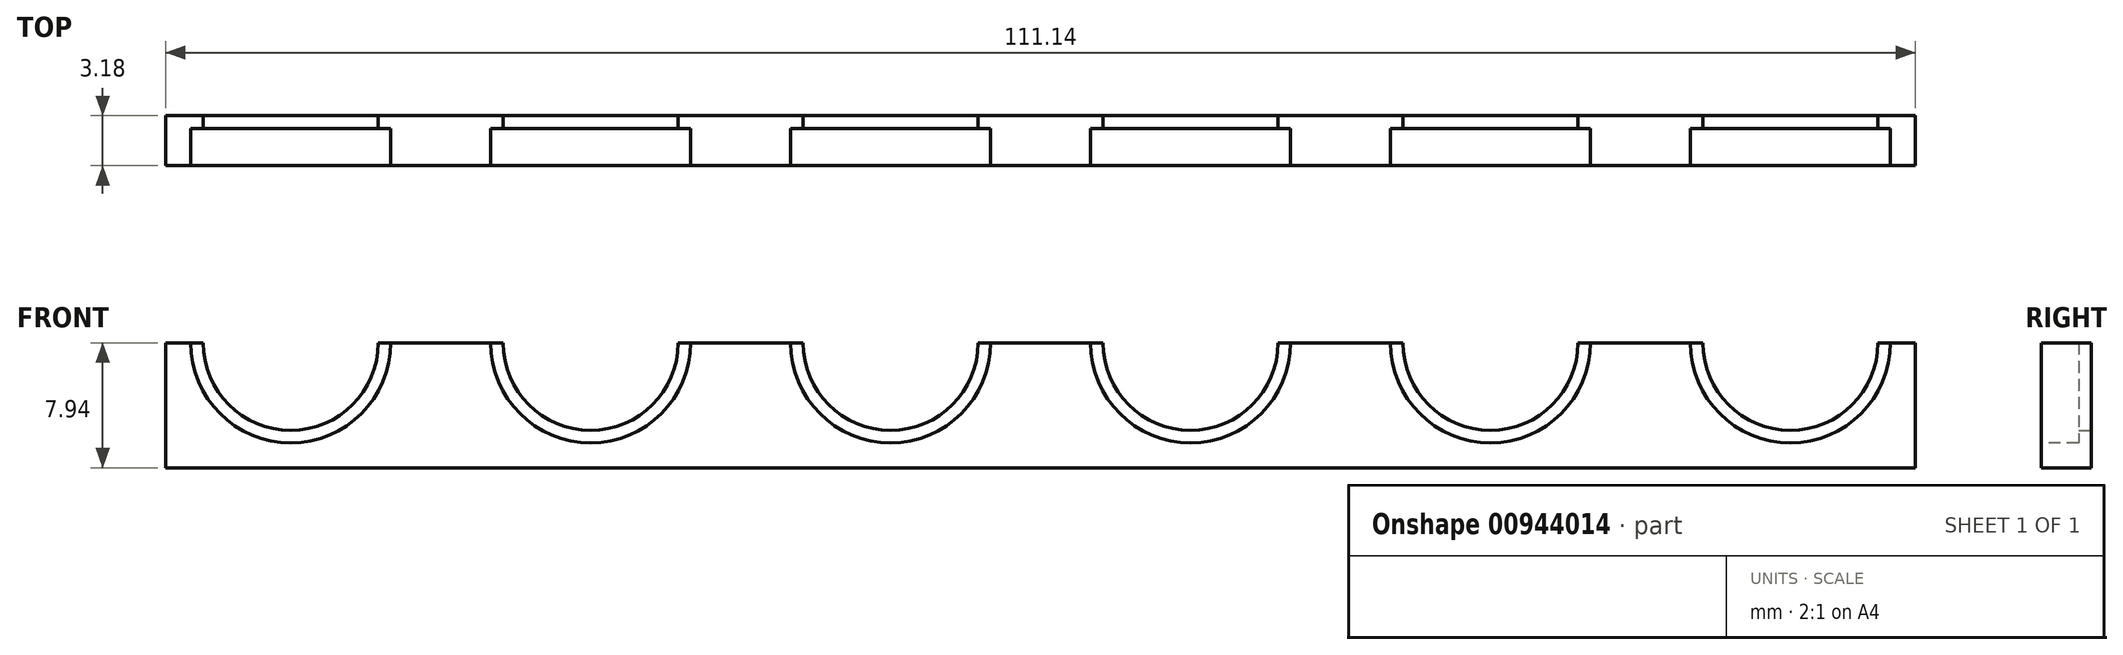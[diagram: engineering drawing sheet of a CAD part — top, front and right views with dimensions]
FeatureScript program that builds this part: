
annotation { "Feature Type Name" : "Feature", "Feature Type Description" : "" }
export const myFeature = defineFeature(function(context is Context, id is Id, definition is map)
    precondition{}
    {
        {
            var Q0;
            Q0=qCreatedBy(makeId("Front.planeOp"),FACE);
            var sketch = newSketch(context, id + "F0", { "sketchPlane" : qUnion([Q0])});
            skLineSegment(sketch, "E0", {"start": v(0, 0) * mm, "end": v(-6.35, 0) * mm});
            skLineSegment(sketch, "E1", {"start": v(-6.35, 0) * mm, "end": v(-7.94, 0) * mm});
            skLineSegment(sketch, "E2", {"start": v(-7.94, 0) * mm, "end": v(-11.11, 0) * mm});
            skLineSegment(sketch, "E3", {"start": v(-11.11, 0) * mm, "end": v(-12.7, 0) * mm});
            skLineSegment(sketch, "E4", {"start": v(-12.7, 0) * mm, "end": v(-19.05, 0) * mm});
            skLineSegment(sketch, "E5", {"start": v(-19.05, 0) * mm, "end": v(-25.4, 0) * mm});
            skLineSegment(sketch, "E6", {"start": v(-25.4, 0) * mm, "end": v(-26.99, 0) * mm});
            skLineSegment(sketch, "E7", {"start": v(-26.99, 0) * mm, "end": v(-30.16, 0) * mm});
            skLineSegment(sketch, "E8", {"start": v(-30.16, 0) * mm, "end": v(-31.75, 0) * mm});
            skLineSegment(sketch, "E9", {"start": v(-31.75, 0) * mm, "end": v(-38.1, 0) * mm});
            skLineSegment(sketch, "E10", {"start": v(-38.1, 0) * mm, "end": v(-44.45, 0) * mm});
            skLineSegment(sketch, "E11", {"start": v(-44.45, 0) * mm, "end": v(-46.04, 0) * mm});
            skLineSegment(sketch, "E12", {"start": v(-46.04, 0) * mm, "end": v(-49.21, 0) * mm});
            skLineSegment(sketch, "E13", {"start": v(-49.21, 0) * mm, "end": v(-50.8, 0) * mm});
            skLineSegment(sketch, "E14", {"start": v(-50.8, 0) * mm, "end": v(-57.15, 0) * mm});
            skLineSegment(sketch, "E15", {"start": v(-57.15, 0) * mm, "end": v(-63.5, 0) * mm});
            skLineSegment(sketch, "E16", {"start": v(-63.5, 0) * mm, "end": v(-65.09, 0) * mm});
            skLineSegment(sketch, "E17", {"start": v(-65.09, 0) * mm, "end": v(-68.26, 0) * mm});
            skLineSegment(sketch, "E18", {"start": v(-68.26, 0) * mm, "end": v(-69.85, 0) * mm});
            skLineSegment(sketch, "E19", {"start": v(-69.85, 0) * mm, "end": v(-76.2, 0) * mm});
            skLineSegment(sketch, "E20", {"start": v(-76.2, 0) * mm, "end": v(-82.55, 0) * mm});
            skLineSegment(sketch, "E21", {"start": v(-82.55, 0) * mm, "end": v(-84.14, 0) * mm});
            skLineSegment(sketch, "E22", {"start": v(-84.14, 0) * mm, "end": v(-87.31, 0) * mm});
            skLineSegment(sketch, "E23", {"start": v(-87.31, 0) * mm, "end": v(-88.9, 0) * mm});
            skLineSegment(sketch, "E24", {"start": v(-88.9, 0) * mm, "end": v(-95.25, 0) * mm});
            skLineSegment(sketch, "E25", {"start": v(-95.25, 0) * mm, "end": v(-101.6, 0) * mm});
            skLineSegment(sketch, "E26", {"start": v(-101.6, 0) * mm, "end": v(-103.2, 0) * mm});
            skLineSegment(sketch, "E27", {"start": v(0, 0) * mm, "end": v(6.35, 0) * mm});
            skLineSegment(sketch, "E28", {"start": v(6.35, 0) * mm, "end": v(7.94, 0) * mm});
            skCircle(sketch, "E29", {"center": v(0, 0) * mm, "radius": 6.35 * mm});
            skCircle(sketch, "E30", {"center": v(0, 0) * mm, "radius": 7.94 * mm});
            skCircle(sketch, "E31", {"center": v(-19.05, 0) * mm, "radius": 6.35 * mm});
            skCircle(sketch, "E32", {"center": v(-19.05, 0) * mm, "radius": 7.94 * mm});
            skCircle(sketch, "E33", {"center": v(-38.1, 0) * mm, "radius": 6.35 * mm});
            skCircle(sketch, "E34", {"center": v(-38.1, 0) * mm, "radius": 7.94 * mm});
            skCircle(sketch, "E35", {"center": v(-57.15, 0) * mm, "radius": 6.35 * mm});
            skCircle(sketch, "E36", {"center": v(-57.15, 0) * mm, "radius": 7.94 * mm});
            skCircle(sketch, "E37", {"center": v(-76.2, 0) * mm, "radius": 6.35 * mm});
            skCircle(sketch, "E38", {"center": v(-76.2, 0) * mm, "radius": 7.94 * mm});
            skCircle(sketch, "E39", {"center": v(-95.25, 0) * mm, "radius": 6.35 * mm});
            skCircle(sketch, "E40", {"center": v(-95.25, 0) * mm, "radius": 7.94 * mm});
            skLineSegment(sketch, "E41", {"start": v(-95.25, 0) * mm, "end": v(-95.25, -7.94) * mm});
            skLineSegment(sketch, "E42", {"start": v(0, 0) * mm, "end": v(0, -7.94) * mm});
            skLineSegment(sketch, "E43", {"start": v(-103.2, 0) * mm, "end": v(-103.2, -7.94) * mm});
            skLineSegment(sketch, "E44", {"start": v(7.94, 0) * mm, "end": v(7.94, -7.94) * mm});
            skLineSegment(sketch, "E45", {"start": v(7.94, -7.94) * mm, "end": v(-103.2, -7.94) * mm});
            skLineSegment(sketch, "E46", {"start": v(-101.6, 0) * mm, "end": v(-100.8, 0) * mm});
            skCircle(sketch, "E47", {"center": v(-95.25, 0) * mm, "radius": 5.56 * mm});
            skLineSegment(sketch, "E48", {"start": v(-82.55, 0) * mm, "end": v(-81.76, 0) * mm});
            skCircle(sketch, "E49", {"center": v(-76.2, 0) * mm, "radius": 5.56 * mm});
            skLineSegment(sketch, "E50", {"start": v(-63.5, 0) * mm, "end": v(-62.7, 0) * mm});
            skCircle(sketch, "E51", {"center": v(-57.15, 0) * mm, "radius": 5.56 * mm});
            skLineSegment(sketch, "E52", {"start": v(-44.45, 0) * mm, "end": v(-43.66, 0) * mm});
            skCircle(sketch, "E53", {"center": v(-38.1, 0) * mm, "radius": 5.56 * mm});
            skLineSegment(sketch, "E54", {"start": v(-25.4, 0) * mm, "end": v(-24.6, 0) * mm});
            skCircle(sketch, "E55", {"center": v(-19.05, 0) * mm, "radius": 5.56 * mm});
            skLineSegment(sketch, "E56", {"start": v(-6.35, 0) * mm, "end": v(-5.56, 0) * mm});
            skCircle(sketch, "E57", {"center": v(0, 0) * mm, "radius": 5.56 * mm});
            skSolve(sketch);
        }
        {
            var Q0;
            {var subQ0=sQuery(id+"F0.wireOp",EDGE,"E43");Q0=makeQuery(id+"F0.imprint","IMPRINT",FACE,{"disambiguationData":[TD([[makeQuery(id+"F0.imprint","IMPRINT",EDGE,{"derivedFrom":subQ0}),1.0]])]});}
            var Q1;
            {var subQ0=sQuery(id+"F0.wireOp",EDGE,"E44");Q1=makeQuery(id+"F0.imprint","IMPRINT",FACE,{"disambiguationData":[TD([[makeQuery(id+"F0.imprint","IMPRINT",EDGE,{"derivedFrom":subQ0}),-1.0]])]});}
            var Q2;
            {var subQ0=sQuery(id+"F0.wireOp",EDGE,"E2");Q2=makeQuery(id+"F0.imprint","IMPRINT",FACE,{"disambiguationData":[TD([[makeQuery(id+"F0.imprint","IMPRINT",EDGE,{"derivedFrom":subQ0}),1.0]])]});}
            var Q3;
            {var subQ0=sQuery(id+"F0.wireOp",EDGE,"E7");Q3=makeQuery(id+"F0.imprint","IMPRINT",FACE,{"disambiguationData":[TD([[makeQuery(id+"F0.imprint","IMPRINT",EDGE,{"derivedFrom":subQ0}),1.0]])]});}
            var Q4;
            {var subQ0=sQuery(id+"F0.wireOp",EDGE,"E12");Q4=makeQuery(id+"F0.imprint","IMPRINT",FACE,{"disambiguationData":[TD([[makeQuery(id+"F0.imprint","IMPRINT",EDGE,{"derivedFrom":subQ0}),1.0]])]});}
            var Q5;
            {var subQ0=sQuery(id+"F0.wireOp",EDGE,"E17");Q5=makeQuery(id+"F0.imprint","IMPRINT",FACE,{"disambiguationData":[TD([[makeQuery(id+"F0.imprint","IMPRINT",EDGE,{"derivedFrom":subQ0}),1.0]])]});}
            var Q6;
            {var subQ0=sQuery(id+"F0.wireOp",EDGE,"E22");Q6=makeQuery(id+"F0.imprint","IMPRINT",FACE,{"disambiguationData":[TD([[makeQuery(id+"F0.imprint","IMPRINT",EDGE,{"derivedFrom":subQ0}),1.0]])]});}
            var Q7;
            {var subQ0=sQuery(id+"F0.wireOp",EDGE,"E1");Q7=makeQuery(id+"F0.imprint","IMPRINT",FACE,{"disambiguationData":[TD([[makeQuery(id+"F0.imprint","IMPRINT",EDGE,{"derivedFrom":subQ0}),1.0]])]});}
            var Q8;
            {var subQ1=sQuery(id+"F0.wireOp",EDGE,"E3");Q8=makeQuery(id+"F0.imprint","IMPRINT",FACE,{"disambiguationData":[TD([[makeQuery(id+"F0.imprint","IMPRINT",EDGE,{"derivedFrom":subQ1}),1.0]])]});}
            var Q9;
            {var subQ1=sQuery(id+"F0.wireOp",EDGE,"E8");Q9=makeQuery(id+"F0.imprint","IMPRINT",FACE,{"disambiguationData":[TD([[makeQuery(id+"F0.imprint","IMPRINT",EDGE,{"derivedFrom":subQ1}),1.0]])]});}
            var Q10;
            {var subQ1=sQuery(id+"F0.wireOp",EDGE,"E13");Q10=makeQuery(id+"F0.imprint","IMPRINT",FACE,{"disambiguationData":[TD([[makeQuery(id+"F0.imprint","IMPRINT",EDGE,{"derivedFrom":subQ1}),1.0]])]});}
            var Q11;
            {var subQ1=sQuery(id+"F0.wireOp",EDGE,"E18");Q11=makeQuery(id+"F0.imprint","IMPRINT",FACE,{"disambiguationData":[TD([[makeQuery(id+"F0.imprint","IMPRINT",EDGE,{"derivedFrom":subQ1}),1.0]])]});}
            var Q12;
            {var subQ0=sQuery(id+"F0.wireOp",EDGE,"E23");Q12=makeQuery(id+"F0.imprint","IMPRINT",FACE,{"disambiguationData":[TD([[makeQuery(id+"F0.imprint","IMPRINT",EDGE,{"derivedFrom":subQ0}),1.0]])]});}
            var Q13;
            {var subQ1=sQuery(id+"F0.wireOp",EDGE,"E26");var subQ3=sQuery(id+"F0.wireOp",EDGE,"E40");var subQ4=makeQuery(id+"F0.imprint","INTERSECT",VERTEX,{"derivedFrom":[subQ1,subQ3]});Q13=makeQuery(id+"F0.imprint","IMPRINT",FACE,{"disambiguationData":[TD([[makeQuery(id+"F0.imprint","IMPRINT",EDGE,{"disambiguationData":[TD([[subQ4,1.0]])],"derivedFrom":subQ1}),1.0]])]});}
            var Q14;
            {var subQ0=sQuery(id+"F0.wireOp",EDGE,"E28");Q14=makeQuery(id+"F0.imprint","IMPRINT",FACE,{"disambiguationData":[TD([[makeQuery(id+"F0.imprint","IMPRINT",EDGE,{"derivedFrom":subQ0}),-1.0]])]});}
            var Q15;
            {var subQ1=sQuery(id+"F0.wireOp",EDGE,"E19");var subQ3=sQuery(id+"F0.wireOp",EDGE,"E49");var subQ4=makeQuery(id+"F0.imprint","INTERSECT",VERTEX,{"derivedFrom":[subQ1,subQ3]});Q15=makeQuery(id+"F0.imprint","IMPRINT",FACE,{"disambiguationData":[TD([[makeQuery(id+"F0.imprint","IMPRINT",EDGE,{"disambiguationData":[TD([[subQ4,1.0]])],"derivedFrom":subQ3}),-1.0]])]});}
            var Q16;
            {var subQ1=sQuery(id+"F0.wireOp",EDGE,"E14");var subQ3=sQuery(id+"F0.wireOp",EDGE,"E51");var subQ4=makeQuery(id+"F0.imprint","INTERSECT",VERTEX,{"derivedFrom":[subQ1,subQ3]});Q16=makeQuery(id+"F0.imprint","IMPRINT",FACE,{"disambiguationData":[TD([[makeQuery(id+"F0.imprint","IMPRINT",EDGE,{"disambiguationData":[TD([[subQ4,1.0]])],"derivedFrom":subQ3}),-1.0]])]});}
            var Q17;
            {var subQ1=sQuery(id+"F0.wireOp",EDGE,"E9");var subQ3=sQuery(id+"F0.wireOp",EDGE,"E53");var subQ4=makeQuery(id+"F0.imprint","INTERSECT",VERTEX,{"derivedFrom":[subQ1,subQ3]});Q17=makeQuery(id+"F0.imprint","IMPRINT",FACE,{"disambiguationData":[TD([[makeQuery(id+"F0.imprint","IMPRINT",EDGE,{"disambiguationData":[TD([[subQ4,1.0]])],"derivedFrom":subQ3}),-1.0]])]});}
            var Q18;
            {var subQ1=sQuery(id+"F0.wireOp",EDGE,"E4");var subQ3=sQuery(id+"F0.wireOp",EDGE,"E55");var subQ4=makeQuery(id+"F0.imprint","INTERSECT",VERTEX,{"derivedFrom":[subQ1,subQ3]});Q18=makeQuery(id+"F0.imprint","IMPRINT",FACE,{"disambiguationData":[TD([[makeQuery(id+"F0.imprint","IMPRINT",EDGE,{"disambiguationData":[TD([[subQ4,1.0]])],"derivedFrom":subQ3}),-1.0]])]});}
            var Q19;
            {var subQ0=sQuery(id+"F0.wireOp",EDGE,"E29");var subQ5=sQuery(id+"F0.wireOp",EDGE,"E42");var subQ6=makeQuery(id+"F0.imprint","INTERSECT",VERTEX,{"derivedFrom":[subQ0,subQ5]});Q19=makeQuery(id+"F0.imprint","IMPRINT",FACE,{"disambiguationData":[TD([[makeQuery(id+"F0.imprint","IMPRINT",EDGE,{"disambiguationData":[TD([[subQ6,1.0]])],"derivedFrom":subQ5}),-1.0]])]});}
            var Q20;
            {var subQ0=sQuery(id+"F0.wireOp",EDGE,"E29");var subQ5=sQuery(id+"F0.wireOp",EDGE,"E42");var subQ7=makeQuery(id+"F0.imprint","INTERSECT",VERTEX,{"derivedFrom":[subQ0,subQ5]});Q20=makeQuery(id+"F0.imprint","IMPRINT",FACE,{"disambiguationData":[TD([[makeQuery(id+"F0.imprint","IMPRINT",EDGE,{"disambiguationData":[TD([[subQ7,1.0]])],"derivedFrom":subQ5}),1.0]])]});}
            var Q21;
            {var subQ0=sQuery(id+"F0.wireOp",EDGE,"E39");var subQ5=sQuery(id+"F0.wireOp",EDGE,"E41");var subQ7=makeQuery(id+"F0.imprint","INTERSECT",VERTEX,{"derivedFrom":[subQ0,subQ5]});Q21=makeQuery(id+"F0.imprint","IMPRINT",FACE,{"disambiguationData":[TD([[makeQuery(id+"F0.imprint","IMPRINT",EDGE,{"disambiguationData":[TD([[subQ7,1.0]])],"derivedFrom":subQ5}),1.0]])]});}
            var Q22;
            {var subQ0=sQuery(id+"F0.wireOp",EDGE,"E39");var subQ5=sQuery(id+"F0.wireOp",EDGE,"E41");var subQ6=makeQuery(id+"F0.imprint","INTERSECT",VERTEX,{"derivedFrom":[subQ0,subQ5]});Q22=makeQuery(id+"F0.imprint","IMPRINT",FACE,{"disambiguationData":[TD([[makeQuery(id+"F0.imprint","IMPRINT",EDGE,{"disambiguationData":[TD([[subQ6,1.0]])],"derivedFrom":subQ5}),-1.0]])]});}
            extrude(context, id + "F1", {"entities" : qUnion([Q0, Q1, Q2, Q3, Q4, Q5, Q6, Q7, Q8, Q9, Q10, Q11, Q12, Q13, Q14, Q15, Q16, Q17, Q18, Q19, Q20, Q21, Q22]), "depth" : 3.17 * mm, "offsetDistance" : 25.4 * mm});
        }
        {
            var Q0;
            Q0=makeQuery(id+"F1.opExtrude","CAP_FACE",FACE,{"disambiguationData":[OSD([sQuery(id+"F0.wireOp",EDGE,"E0"),sQuery(id+"F0.wireOp",EDGE,"E1"),sQuery(id+"F0.wireOp",EDGE,"E2"),sQuery(id+"F0.wireOp",EDGE,"E3"),sQuery(id+"F0.wireOp",EDGE,"E4"),sQuery(id+"F0.wireOp",EDGE,"E5"),sQuery(id+"F0.wireOp",EDGE,"E6"),sQuery(id+"F0.wireOp",EDGE,"E7"),sQuery(id+"F0.wireOp",EDGE,"E8"),sQuery(id+"F0.wireOp",EDGE,"E9"),sQuery(id+"F0.wireOp",EDGE,"E10"),sQuery(id+"F0.wireOp",EDGE,"E11"),sQuery(id+"F0.wireOp",EDGE,"E12"),sQuery(id+"F0.wireOp",EDGE,"E13"),sQuery(id+"F0.wireOp",EDGE,"E14"),sQuery(id+"F0.wireOp",EDGE,"E15"),sQuery(id+"F0.wireOp",EDGE,"E16"),sQuery(id+"F0.wireOp",EDGE,"E17"),sQuery(id+"F0.wireOp",EDGE,"E18"),sQuery(id+"F0.wireOp",EDGE,"E19"),sQuery(id+"F0.wireOp",EDGE,"E20"),sQuery(id+"F0.wireOp",EDGE,"E21"),sQuery(id+"F0.wireOp",EDGE,"E22"),sQuery(id+"F0.wireOp",EDGE,"E23"),sQuery(id+"F0.wireOp",EDGE,"E24"),sQuery(id+"F0.wireOp",EDGE,"E25"),sQuery(id+"F0.wireOp",EDGE,"E26"),sQuery(id+"F0.wireOp",EDGE,"E27"),sQuery(id+"F0.wireOp",EDGE,"E28"),sQuery(id+"F0.wireOp",EDGE,"E43"),sQuery(id+"F0.wireOp",EDGE,"E44"),sQuery(id+"F0.wireOp",EDGE,"E45"),sQuery(id+"F0.wireOp",EDGE,"E47"),sQuery(id+"F0.wireOp",EDGE,"E49"),sQuery(id+"F0.wireOp",EDGE,"E51"),sQuery(id+"F0.wireOp",EDGE,"E53"),sQuery(id+"F0.wireOp",EDGE,"E55"),sQuery(id+"F0.wireOp",EDGE,"E57")])],"isStart":false});
            var sketch = newSketch(context, id + "F2", { "sketchPlane" : qUnion([Q0])});
            skLineSegment(sketch, "E58", {"start": v(-100.8, 0) * mm, "end": v(-101.6, 0) * mm});
            skCircle(sketch, "E59", {"center": v(-95.25, 0) * mm, "radius": 6.35 * mm});
            skLineSegment(sketch, "E60", {"start": v(-81.76, 0) * mm, "end": v(-82.55, 0) * mm});
            skCircle(sketch, "E61", {"center": v(-76.2, 0) * mm, "radius": 6.35 * mm});
            skLineSegment(sketch, "E62", {"start": v(-62.7, 0) * mm, "end": v(-63.5, 0) * mm});
            skCircle(sketch, "E63", {"center": v(-57.15, 0) * mm, "radius": 6.35 * mm});
            skLineSegment(sketch, "E64", {"start": v(-43.66, 0) * mm, "end": v(-44.45, 0) * mm});
            skCircle(sketch, "E65", {"center": v(-38.1, 0) * mm, "radius": 6.35 * mm});
            skLineSegment(sketch, "E66", {"start": v(-24.6, 0) * mm, "end": v(-25.4, 0) * mm});
            skCircle(sketch, "E67", {"center": v(-19.05, 0) * mm, "radius": 6.35 * mm});
            skLineSegment(sketch, "E68", {"start": v(-5.56, 0) * mm, "end": v(-6.35, 0) * mm});
            skCircle(sketch, "E69", {"center": v(0, 0) * mm, "radius": 6.35 * mm});
            skSolve(sketch);
        }
        {
            var Q0;
            Q0 = qSketchRegion(id + "F2", true);
            extrude(context, id + "F3", {"entities" : qUnion([Q0]), "operationType" : NewBodyOperationType.REMOVE, "oppositeDirection" : true, "depth" : 2.36 * mm, "offsetDistance" : 25.4 * mm});
        }
        {
            var Q0;
            Q0=makeQuery(id+"F1.opExtrude","SWEPT_FACE",FACE,{"disambiguationData":[OSD([sQuery(id+"F0.wireOp",EDGE,"E44")])]});
            var sketch = newSketch(context, id + "F4", { "sketchPlane" : qUnion([Q0])});
            skLineSegment(sketch, "E70", {"start": v(-3.18, 0) * mm, "end": v(-2.38, 0) * mm});
            skLineSegment(sketch, "E71", {"start": v(-2.38, 0) * mm, "end": v(-2.38, -3.18) * mm});
            skLineSegment(sketch, "E72", {"start": v(-2.38, -3.18) * mm, "end": v(-2.38, -4.76) * mm});
            skLineSegment(sketch, "E73", {"start": v(-2.38, -4.76) * mm, "end": v(-0.8, -4.76) * mm});
            skLineSegment(sketch, "E74", {"start": v(-0.8, -4.76) * mm, "end": v(-0.8, -3.18) * mm});
            skLineSegment(sketch, "E75", {"start": v(-0.8, -3.18) * mm, "end": v(-2.38, -3.18) * mm});
            skLineSegment(sketch, "E76", {"start": v(-0.8, -3.18) * mm, "end": v(-0.8, 0) * mm});
            skLineSegment(sketch, "E77", {"start": v(-0.8, 0) * mm, "end": v(0, 0) * mm});
            skLineSegment(sketch, "E78", {"start": v(0, 0) * mm, "end": v(0, -7.94) * mm});
            skLineSegment(sketch, "E79", {"start": v(0, -7.94) * mm, "end": v(-3.18, -7.94) * mm});
            skLineSegment(sketch, "E80", {"start": v(-3.18, -7.94) * mm, "end": v(-3.18, 0) * mm});
            skSolve(sketch);
        }
        {
            var Q0;
            Q0=makeQuery(id+"F4.imprint","IMPRINT",FACE,{"disambiguationData":[TD([[makeQuery(id+"F4.imprint","IMPRINT",EDGE,{"derivedFrom":sQuery(id+"F4.wireOp",EDGE,"E70")}),-1.0]])]});
            extrude(context, id + "F5", {"entities" : qUnion([Q0]), "operationType" : NewBodyOperationType.ADD, "depth" : 1.59 * mm, "offsetDistance" : 25.4 * mm});
        }
        {
            var Q0;
            Q0=makeQuery(id+"F1.opExtrude","SWEPT_FACE",FACE,{"disambiguationData":[OSD([sQuery(id+"F0.wireOp",EDGE,"E43")])]});
            var sketch = newSketch(context, id + "F6", { "sketchPlane" : qUnion([Q0])});
            skLineSegment(sketch, "E81", {"start": v(0, 0) * mm, "end": v(0.8, 0) * mm});
            skLineSegment(sketch, "E82", {"start": v(0.8, 0) * mm, "end": v(0.8, -3.18) * mm});
            skLineSegment(sketch, "E83", {"start": v(0.8, -3.18) * mm, "end": v(0.8, -4.76) * mm});
            skLineSegment(sketch, "E84", {"start": v(0.8, -4.76) * mm, "end": v(2.38, -4.76) * mm});
            skLineSegment(sketch, "E85", {"start": v(2.38, -4.76) * mm, "end": v(2.38, -3.18) * mm});
            skLineSegment(sketch, "E86", {"start": v(2.38, -3.18) * mm, "end": v(0.8, -3.18) * mm});
            skLineSegment(sketch, "E87", {"start": v(2.38, -3.18) * mm, "end": v(2.38, 0) * mm});
            skLineSegment(sketch, "E88", {"start": v(2.38, 0) * mm, "end": v(3.18, 0) * mm});
            skLineSegment(sketch, "E89", {"start": v(3.18, 0) * mm, "end": v(3.18, -7.94) * mm});
            skLineSegment(sketch, "E90", {"start": v(3.18, -7.94) * mm, "end": v(0, -7.94) * mm});
            skLineSegment(sketch, "E91", {"start": v(0, -7.94) * mm, "end": v(0, 0) * mm});
            skSolve(sketch);
        }
        {
            var Q0;
            Q0=makeQuery(id+"F6.imprint","IMPRINT",FACE,{"disambiguationData":[TD([[makeQuery(id+"F6.imprint","IMPRINT",EDGE,{"derivedFrom":sQuery(id+"F6.wireOp",EDGE,"E81")}),1.0]])]});
            extrude(context, id + "F7", {"entities" : qUnion([Q0]), "operationType" : NewBodyOperationType.ADD, "depth" : 1.59 * mm, "offsetDistance" : 25.4 * mm});
        }
        {
            var Q0;
            Q0=makeQuery(id+"F7.boolean.opBoolean","MERGE",FACE,{"derivedFrom":[makeQuery(id+"F5.boolean.opBoolean","MERGE",FACE,{"derivedFrom":[makeQuery(id+"F1.opExtrude","CAP_FACE",FACE,{"disambiguationData":[OSD([sQuery(id+"F0.wireOp",EDGE,"E0"),sQuery(id+"F0.wireOp",EDGE,"E1"),sQuery(id+"F0.wireOp",EDGE,"E2"),sQuery(id+"F0.wireOp",EDGE,"E3"),sQuery(id+"F0.wireOp",EDGE,"E4"),sQuery(id+"F0.wireOp",EDGE,"E5"),sQuery(id+"F0.wireOp",EDGE,"E6"),sQuery(id+"F0.wireOp",EDGE,"E7"),sQuery(id+"F0.wireOp",EDGE,"E8"),sQuery(id+"F0.wireOp",EDGE,"E9"),sQuery(id+"F0.wireOp",EDGE,"E10"),sQuery(id+"F0.wireOp",EDGE,"E11"),sQuery(id+"F0.wireOp",EDGE,"E12"),sQuery(id+"F0.wireOp",EDGE,"E13"),sQuery(id+"F0.wireOp",EDGE,"E14"),sQuery(id+"F0.wireOp",EDGE,"E15"),sQuery(id+"F0.wireOp",EDGE,"E16"),sQuery(id+"F0.wireOp",EDGE,"E17"),sQuery(id+"F0.wireOp",EDGE,"E18"),sQuery(id+"F0.wireOp",EDGE,"E19"),sQuery(id+"F0.wireOp",EDGE,"E20"),sQuery(id+"F0.wireOp",EDGE,"E21"),sQuery(id+"F0.wireOp",EDGE,"E22"),sQuery(id+"F0.wireOp",EDGE,"E23"),sQuery(id+"F0.wireOp",EDGE,"E24"),sQuery(id+"F0.wireOp",EDGE,"E25"),sQuery(id+"F0.wireOp",EDGE,"E26"),sQuery(id+"F0.wireOp",EDGE,"E27"),sQuery(id+"F0.wireOp",EDGE,"E28"),sQuery(id+"F0.wireOp",EDGE,"E43"),sQuery(id+"F0.wireOp",EDGE,"E44"),sQuery(id+"F0.wireOp",EDGE,"E45"),sQuery(id+"F0.wireOp",EDGE,"E47"),sQuery(id+"F0.wireOp",EDGE,"E49"),sQuery(id+"F0.wireOp",EDGE,"E51"),sQuery(id+"F0.wireOp",EDGE,"E53"),sQuery(id+"F0.wireOp",EDGE,"E55"),sQuery(id+"F0.wireOp",EDGE,"E57")])],"isStart":true}),makeQuery(id+"F5.opExtrude","SWEPT_FACE",FACE,{"disambiguationData":[OSD([sQuery(id+"F4.wireOp",EDGE,"E78")])]})]}),makeQuery(id+"F7.opExtrude","SWEPT_FACE",FACE,{"disambiguationData":[OSD([sQuery(id+"F6.wireOp",EDGE,"E91")])]})]});
            var sketch = newSketch(context, id + "F8", { "sketchPlane" : qUnion([Q0])});
            skLineSegment(sketch, "E92", {"start": v(-9.53, 0) * mm, "end": v(-7.94, 0) * mm});
            skLineSegment(sketch, "E93", {"start": v(-7.94, 0) * mm, "end": v(-7.94, -3.17) * mm});
            skLineSegment(sketch, "E94", {"start": v(-7.94, -3.17) * mm, "end": v(-9.53, -3.17) * mm});
            skLineSegment(sketch, "E95", {"start": v(-9.53, -3.17) * mm, "end": v(-7.94, 0) * mm});
            skSolve(sketch);
        }
        {
            var Q0;
            Q0 = qSketchRegion(id + "F8", true);
            extrude(context, id + "F9", {"entities" : qUnion([Q0]), "operationType" : NewBodyOperationType.ADD, "oppositeDirection" : true, "depth" : 2.4 * mm, "offsetDistance" : 25.4 * mm});
        }
        {
            var Q0;
            Q0=makeQuery(id+"F7.boolean.opBoolean","MERGE",FACE,{"derivedFrom":[makeQuery(id+"F5.boolean.opBoolean","MERGE",FACE,{"derivedFrom":[makeQuery(id+"F1.opExtrude","CAP_FACE",FACE,{"disambiguationData":[OSD([sQuery(id+"F0.wireOp",EDGE,"E0"),sQuery(id+"F0.wireOp",EDGE,"E1"),sQuery(id+"F0.wireOp",EDGE,"E2"),sQuery(id+"F0.wireOp",EDGE,"E3"),sQuery(id+"F0.wireOp",EDGE,"E4"),sQuery(id+"F0.wireOp",EDGE,"E5"),sQuery(id+"F0.wireOp",EDGE,"E6"),sQuery(id+"F0.wireOp",EDGE,"E7"),sQuery(id+"F0.wireOp",EDGE,"E8"),sQuery(id+"F0.wireOp",EDGE,"E9"),sQuery(id+"F0.wireOp",EDGE,"E10"),sQuery(id+"F0.wireOp",EDGE,"E11"),sQuery(id+"F0.wireOp",EDGE,"E12"),sQuery(id+"F0.wireOp",EDGE,"E13"),sQuery(id+"F0.wireOp",EDGE,"E14"),sQuery(id+"F0.wireOp",EDGE,"E15"),sQuery(id+"F0.wireOp",EDGE,"E16"),sQuery(id+"F0.wireOp",EDGE,"E17"),sQuery(id+"F0.wireOp",EDGE,"E18"),sQuery(id+"F0.wireOp",EDGE,"E19"),sQuery(id+"F0.wireOp",EDGE,"E20"),sQuery(id+"F0.wireOp",EDGE,"E21"),sQuery(id+"F0.wireOp",EDGE,"E22"),sQuery(id+"F0.wireOp",EDGE,"E23"),sQuery(id+"F0.wireOp",EDGE,"E24"),sQuery(id+"F0.wireOp",EDGE,"E25"),sQuery(id+"F0.wireOp",EDGE,"E26"),sQuery(id+"F0.wireOp",EDGE,"E27"),sQuery(id+"F0.wireOp",EDGE,"E28"),sQuery(id+"F0.wireOp",EDGE,"E43"),sQuery(id+"F0.wireOp",EDGE,"E44"),sQuery(id+"F0.wireOp",EDGE,"E45"),sQuery(id+"F0.wireOp",EDGE,"E47"),sQuery(id+"F0.wireOp",EDGE,"E49"),sQuery(id+"F0.wireOp",EDGE,"E51"),sQuery(id+"F0.wireOp",EDGE,"E53"),sQuery(id+"F0.wireOp",EDGE,"E55"),sQuery(id+"F0.wireOp",EDGE,"E57")])],"isStart":true}),makeQuery(id+"F5.opExtrude","SWEPT_FACE",FACE,{"disambiguationData":[OSD([sQuery(id+"F4.wireOp",EDGE,"E78")])]})]}),makeQuery(id+"F7.opExtrude","SWEPT_FACE",FACE,{"disambiguationData":[OSD([sQuery(id+"F6.wireOp",EDGE,"E91")])]})]});
            var sketch = newSketch(context, id + "F10", { "sketchPlane" : qUnion([Q0])});
            skLineSegment(sketch, "E96", {"start": v(104.79, 0) * mm, "end": v(104, 0) * mm});
            skLineSegment(sketch, "E97", {"start": v(104, 0) * mm, "end": v(104, -3.18) * mm});
            skLineSegment(sketch, "E98", {"start": v(104, -3.18) * mm, "end": v(104.79, -3.18) * mm});
            skLineSegment(sketch, "E99", {"start": v(104, 0) * mm, "end": v(104.79, -3.18) * mm});
            skSolve(sketch);
        }
        {
            var Q0;
            Q0 = qSketchRegion(id + "F10", true);
            extrude(context, id + "F11", {"entities" : qUnion([Q0]), "operationType" : NewBodyOperationType.ADD, "oppositeDirection" : true, "depth" : 2.4 * mm, "offsetDistance" : 25.4 * mm});
        }
        {
            var Q0;
            Q0=makeQuery(id+"F7.boolean.opBoolean","MERGE",FACE,{"derivedFrom":[makeQuery(id+"F5.boolean.opBoolean","MERGE",FACE,{"derivedFrom":[makeQuery(id+"F1.opExtrude","CAP_FACE",FACE,{"disambiguationData":[OSD([sQuery(id+"F0.wireOp",EDGE,"E0"),sQuery(id+"F0.wireOp",EDGE,"E1"),sQuery(id+"F0.wireOp",EDGE,"E2"),sQuery(id+"F0.wireOp",EDGE,"E3"),sQuery(id+"F0.wireOp",EDGE,"E4"),sQuery(id+"F0.wireOp",EDGE,"E5"),sQuery(id+"F0.wireOp",EDGE,"E6"),sQuery(id+"F0.wireOp",EDGE,"E7"),sQuery(id+"F0.wireOp",EDGE,"E8"),sQuery(id+"F0.wireOp",EDGE,"E9"),sQuery(id+"F0.wireOp",EDGE,"E10"),sQuery(id+"F0.wireOp",EDGE,"E11"),sQuery(id+"F0.wireOp",EDGE,"E12"),sQuery(id+"F0.wireOp",EDGE,"E13"),sQuery(id+"F0.wireOp",EDGE,"E14"),sQuery(id+"F0.wireOp",EDGE,"E15"),sQuery(id+"F0.wireOp",EDGE,"E16"),sQuery(id+"F0.wireOp",EDGE,"E17"),sQuery(id+"F0.wireOp",EDGE,"E18"),sQuery(id+"F0.wireOp",EDGE,"E19"),sQuery(id+"F0.wireOp",EDGE,"E20"),sQuery(id+"F0.wireOp",EDGE,"E21"),sQuery(id+"F0.wireOp",EDGE,"E22"),sQuery(id+"F0.wireOp",EDGE,"E23"),sQuery(id+"F0.wireOp",EDGE,"E24"),sQuery(id+"F0.wireOp",EDGE,"E25"),sQuery(id+"F0.wireOp",EDGE,"E26"),sQuery(id+"F0.wireOp",EDGE,"E27"),sQuery(id+"F0.wireOp",EDGE,"E28"),sQuery(id+"F0.wireOp",EDGE,"E43"),sQuery(id+"F0.wireOp",EDGE,"E44"),sQuery(id+"F0.wireOp",EDGE,"E45"),sQuery(id+"F0.wireOp",EDGE,"E47"),sQuery(id+"F0.wireOp",EDGE,"E49"),sQuery(id+"F0.wireOp",EDGE,"E51"),sQuery(id+"F0.wireOp",EDGE,"E53"),sQuery(id+"F0.wireOp",EDGE,"E55"),sQuery(id+"F0.wireOp",EDGE,"E57")])],"isStart":false}),makeQuery(id+"F5.opExtrude","SWEPT_FACE",FACE,{"disambiguationData":[OSD([sQuery(id+"F4.wireOp",EDGE,"E80")])]})]}),makeQuery(id+"F7.opExtrude","SWEPT_FACE",FACE,{"disambiguationData":[OSD([sQuery(id+"F6.wireOp",EDGE,"E89")])]})]});
            var sketch = newSketch(context, id + "F12", { "sketchPlane" : qUnion([Q0])});
            skLineSegment(sketch, "E100", {"start": v(9.53, 0) * mm, "end": v(7.94, 0) * mm});
            skLineSegment(sketch, "E101", {"start": v(7.94, 0) * mm, "end": v(7.94, -7.94) * mm});
            skLineSegment(sketch, "E102", {"start": v(7.94, -7.94) * mm, "end": v(9.53, -7.94) * mm});
            skLineSegment(sketch, "E103", {"start": v(9.53, -7.94) * mm, "end": v(9.53, 0) * mm});
            skLineSegment(sketch, "E104", {"start": v(-104.79, 0) * mm, "end": v(-103.2, 0) * mm});
            skLineSegment(sketch, "E105", {"start": v(-103.2, 0) * mm, "end": v(-103.2, -7.94) * mm});
            skLineSegment(sketch, "E106", {"start": v(-103.2, -7.94) * mm, "end": v(-104.79, -7.94) * mm});
            skLineSegment(sketch, "E107", {"start": v(-104.79, -7.94) * mm, "end": v(-104.79, 0) * mm});
            skSolve(sketch);
        }
        {
            var Q0;
            Q0 = qSketchRegion(id + "F12", true);
            extrude(context, id + "F13", {"entities" : qUnion([Q0]), "operationType" : NewBodyOperationType.REMOVE, "oppositeDirection" : true, "depth" : 25.4 * mm, "offsetDistance" : 25.4 * mm});
        }
    });
